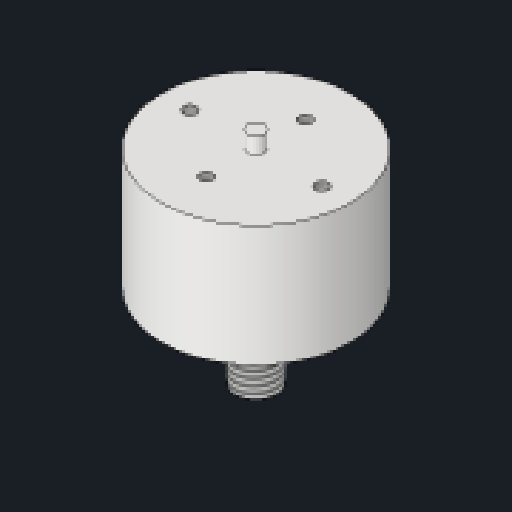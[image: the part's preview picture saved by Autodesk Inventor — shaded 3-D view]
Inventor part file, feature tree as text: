
AUTODESK INVENTOR PART (.ipt)
format: ipt  version: 2023.2 (Build 272271030, 271C)  size: 121,856 bytes
history: native  units: mm
features: sketch x2, revolve x1, thread x1, hole x1
ambient origin geometry x8: Origin, YZ Plane, XZ Plane, XY Plane, X Axis, Y Axis, Z Axis, Center Point
bodies: Solid1 (feature_tree)
feature tree (5):
  revolve  "Revolution1"  [1 undecoded]
  thread  "Thread1"  [1 undecoded]
  hole  "Hole1"  [1 undecoded]
  sketch  "Sketch1"  dims[d0=11.5mm d1=24.7mm d2=2.5mm]
  sketch  "Sketch2"  dims[d3=10.0mm d4=1.0mm d5=2.0mm d6=90.0deg d7=7.0mm d8=3.0mm d9=6.0mm d10=6.0mm d11=8.0mm d12=8.0mm d13=1.567mm d14=4.0mm d15=8.72mm d16=5.0mm d17=90.0deg d18=6.3mm d19=20.594885mm]
note: 3 required parameter values undecoded (feature->parameter linkage not recoverable at this tier; creation-order binding heuristic only, values carry confidence <= 0.55)